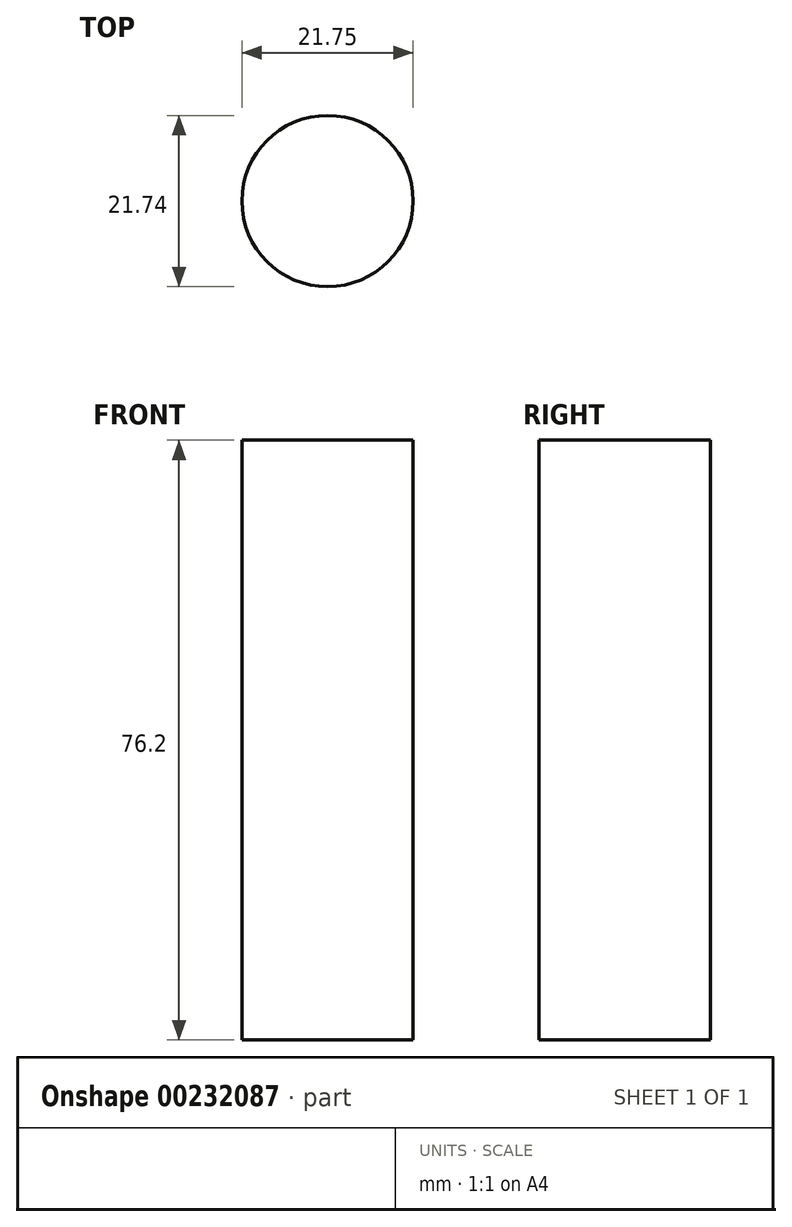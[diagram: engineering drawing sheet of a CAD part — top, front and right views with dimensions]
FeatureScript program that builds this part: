
annotation { "Feature Type Name" : "Feature", "Feature Type Description" : "" }
export const myFeature = defineFeature(function(context is Context, id is Id, definition is map)
    precondition{}
    {
        {
            var Q0;
            Q0=qCreatedBy(makeId("Top.planeOp"),FACE);
            var sketch = newSketch(context, id + "F0", { "sketchPlane" : qUnion([Q0])});
            skCircle(sketch, "E0", {"center": v(-34.35, 32.14) * mm, "radius": 10.87 * mm});
            skSolve(sketch);
        }
        {
            var Q0;
            Q0=makeQuery(id+"F0.imprint","IMPRINT",FACE,{"disambiguationData":[TD([[makeQuery(id+"F0.imprint","IMPRINT",EDGE,{"derivedFrom":sQuery(id+"F0.wireOp",EDGE,"E0")}),1.0]])]});
            var Q1;
            Q1 = qConstructionFilter(qBodyType(qCreatedBy(id + "F0" ,EDGE), BodyType.WIRE), ConstructionObject.NO);
            extrude(context, id + "F1", {"entities" : qUnion([Q0]), "bodyType" : ToolBodyType.SURFACE, "surfaceEntities" : qUnion([Q1]), "depth" : 76.2 * mm});
        }
    });
